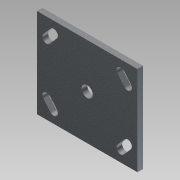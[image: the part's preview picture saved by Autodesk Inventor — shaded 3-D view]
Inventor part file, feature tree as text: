
AUTODESK INVENTOR PART (.ipt)
format: ipt  version: 2012 (Build 160160000, 160)  size: 132,608 bytes
history: native  units: in
note: dims shown in document units (in); Inventor stores cm internally (conversion verified against a paired STEP export)
features: extrude x2, sketch x2
ambient origin geometry x8: Origin, YZ Plane, XZ Plane, XY Plane, X Axis, Y Axis, Z Axis, Center Point
bodies: Solid1 (feature_tree)
feature tree (4):
  extrude  "Extrusion1"  Depth=4.0in
  extrude  "Extrusion2"  Depth=0.375in
  sketch  "Sketch1"  dims[d0=4.5in d1=4.0in]
  sketch  "Sketch2"  dims[d8=0.375in d9=0.375in d10=0.375in d11=1.8125in d14=1.8125in d16=0.375in d20=0.375in d22=0.375in d23=0.25in d24=0.0in d25=0.5in d26=0.25in d27=0.0in]
